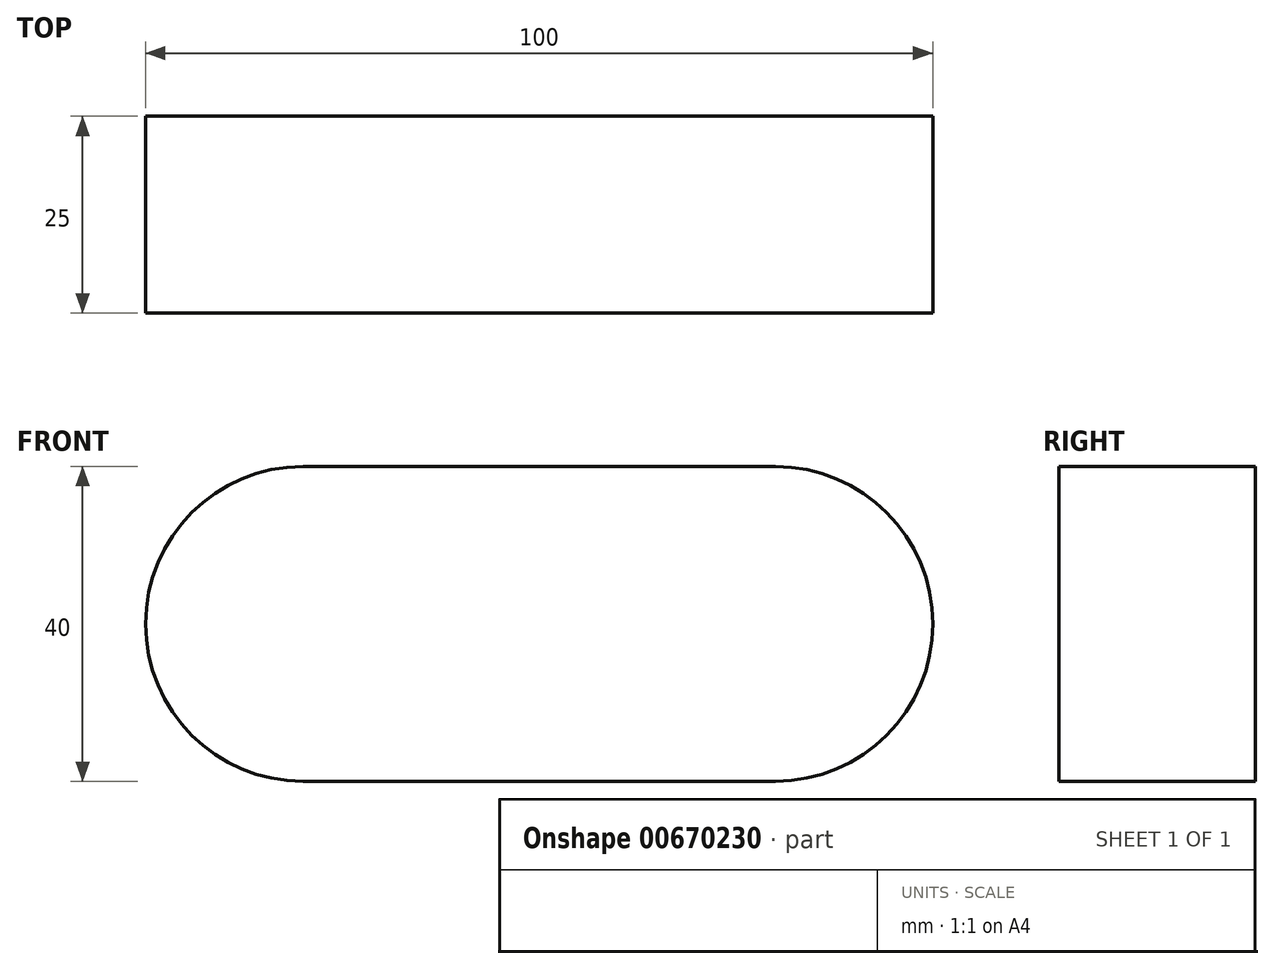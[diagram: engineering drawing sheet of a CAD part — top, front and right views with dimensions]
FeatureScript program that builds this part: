
annotation { "Feature Type Name" : "Feature", "Feature Type Description" : "" }
export const myFeature = defineFeature(function(context is Context, id is Id, definition is map)
    precondition{}
    {
        {
            var Q0;
            Q0=qCreatedBy(makeId("Front.planeOp"),FACE);
            var sketch = newSketch(context, id + "F0", { "sketchPlane" : qUnion([Q0])});
            skLineSegment(sketch, "E0.bottom", {"start": v(-30, 20) * mm, "end": v(30, 20) * mm});
            skLineSegment(sketch, "E0.top", {"start": v(-30, -20) * mm, "end": v(30, -20) * mm});
            skLineSegment(sketch, "E0.left", {"start": v(-30, 20) * mm, "end": v(-30, -20) * mm});
            skLineSegment(sketch, "E0.right", {"start": v(30, 20) * mm, "end": v(30, -20) * mm});
            skCircle(sketch, "E1", {"center": v(30, 0) * mm, "radius": 20 * mm});
            skCircle(sketch, "E2", {"center": v(-30, 0) * mm, "radius": 20 * mm});
            skSolve(sketch);
        }
        {
            var Q0;
            Q0 = qSketchRegion(id + "F0", true);
            extrude(context, id + "F1", {"entities" : qUnion([Q0]), "depth" : 25 * mm, "offsetDistance" : 25 * mm});
        }
    });
